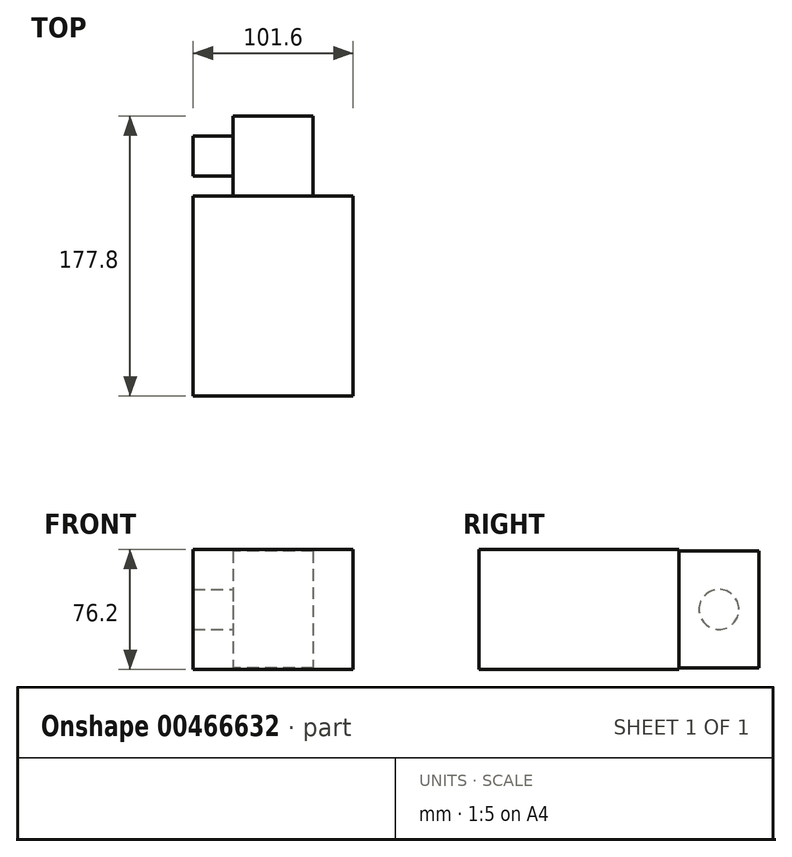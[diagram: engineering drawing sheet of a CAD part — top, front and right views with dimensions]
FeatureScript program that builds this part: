
annotation { "Feature Type Name" : "Feature", "Feature Type Description" : "" }
export const myFeature = defineFeature(function(context is Context, id is Id, definition is map)
    precondition{}
    {
        {
            var Q0;
            Q0=qCreatedBy(makeId("Top.planeOp"),FACE);
            var sketch = newSketch(context, id + "F0", { "sketchPlane" : qUnion([Q0])});
            skLineSegment(sketch, "E0.bottom", {"start": v(25.4, 25.4) * mm, "end": v(-25.4, 25.4) * mm});
            skLineSegment(sketch, "E0.top", {"start": v(25.4, -25.4) * mm, "end": v(-25.4, -25.4) * mm});
            skLineSegment(sketch, "E0.left", {"start": v(25.4, 25.4) * mm, "end": v(25.4, -25.4) * mm});
            skLineSegment(sketch, "E0.right", {"start": v(-25.4, 25.4) * mm, "end": v(-25.4, -25.4) * mm});
            skPoint(sketch, "E0.middle", {"position": v(0, 0) * mm});
            skSolve(sketch);
        }
        {
            var Q0;
            Q0 = qSketchRegion(id + "F0", true);
            extrude(context, id + "F1", {"entities" : qUnion([Q0]), "depth" : 74.22 * mm});
        }
        {
            var Q0;
            Q0=makeQuery(id+"F1.opExtrude","SWEPT_FACE",FACE,{"disambiguationData":[OSD([sQuery(id+"F0.wireOp",EDGE,"E0.right")])]});
            var sketch = newSketch(context, id + "F2", { "sketchPlane" : qUnion([Q0])});
            skCircle(sketch, "E1", {"center": v(0, 37.11) * mm, "radius": 12.7 * mm});
            skPoint(sketch, "E1.centerSnap0", {"position": v(25.4, 37.11) * mm});
            skSolve(sketch);
        }
        {
            var Q0;
            Q0 = qSketchRegion(id + "F2", true);
            extrude(context, id + "F3", {"entities" : qUnion([Q0]), "operationType" : NewBodyOperationType.ADD, "depth" : 25.4 * mm});
        }
        {
            var Q0;
            Q0=makeQuery(id+"F1.opExtrude","SWEPT_FACE",FACE,{"disambiguationData":[OSD([sQuery(id+"F0.wireOp",EDGE,"E0.top")])]});
            var sketch = newSketch(context, id + "F4", { "sketchPlane" : qUnion([Q0])});
            skLineSegment(sketch, "E2.bottom", {"start": v(50.8, 75.21) * mm, "end": v(-50.8, 75.21) * mm});
            skLineSegment(sketch, "E2.top", {"start": v(50.8, -0.99) * mm, "end": v(-50.8, -0.99) * mm});
            skLineSegment(sketch, "E2.left", {"start": v(50.8, 75.21) * mm, "end": v(50.8, -0.99) * mm});
            skLineSegment(sketch, "E2.right", {"start": v(-50.8, 75.21) * mm, "end": v(-50.8, -0.99) * mm});
            skPoint(sketch, "E2.middle", {"position": v(0, 37.11) * mm});
            skPoint(sketch, "E2.middle.positionSnap0", {"position": v(-25.4, 37.11) * mm});
            skPoint(sketch, "E2.centerSnap0", {"position": v(-25.4, 37.11) * mm});
            skSolve(sketch);
        }
        {
            var Q0;
            Q0 = qSketchRegion(id + "F4", true);
            extrude(context, id + "F5", {"entities" : qUnion([Q0]), "operationType" : NewBodyOperationType.ADD, "depth" : 127 * mm});
        }
    });
